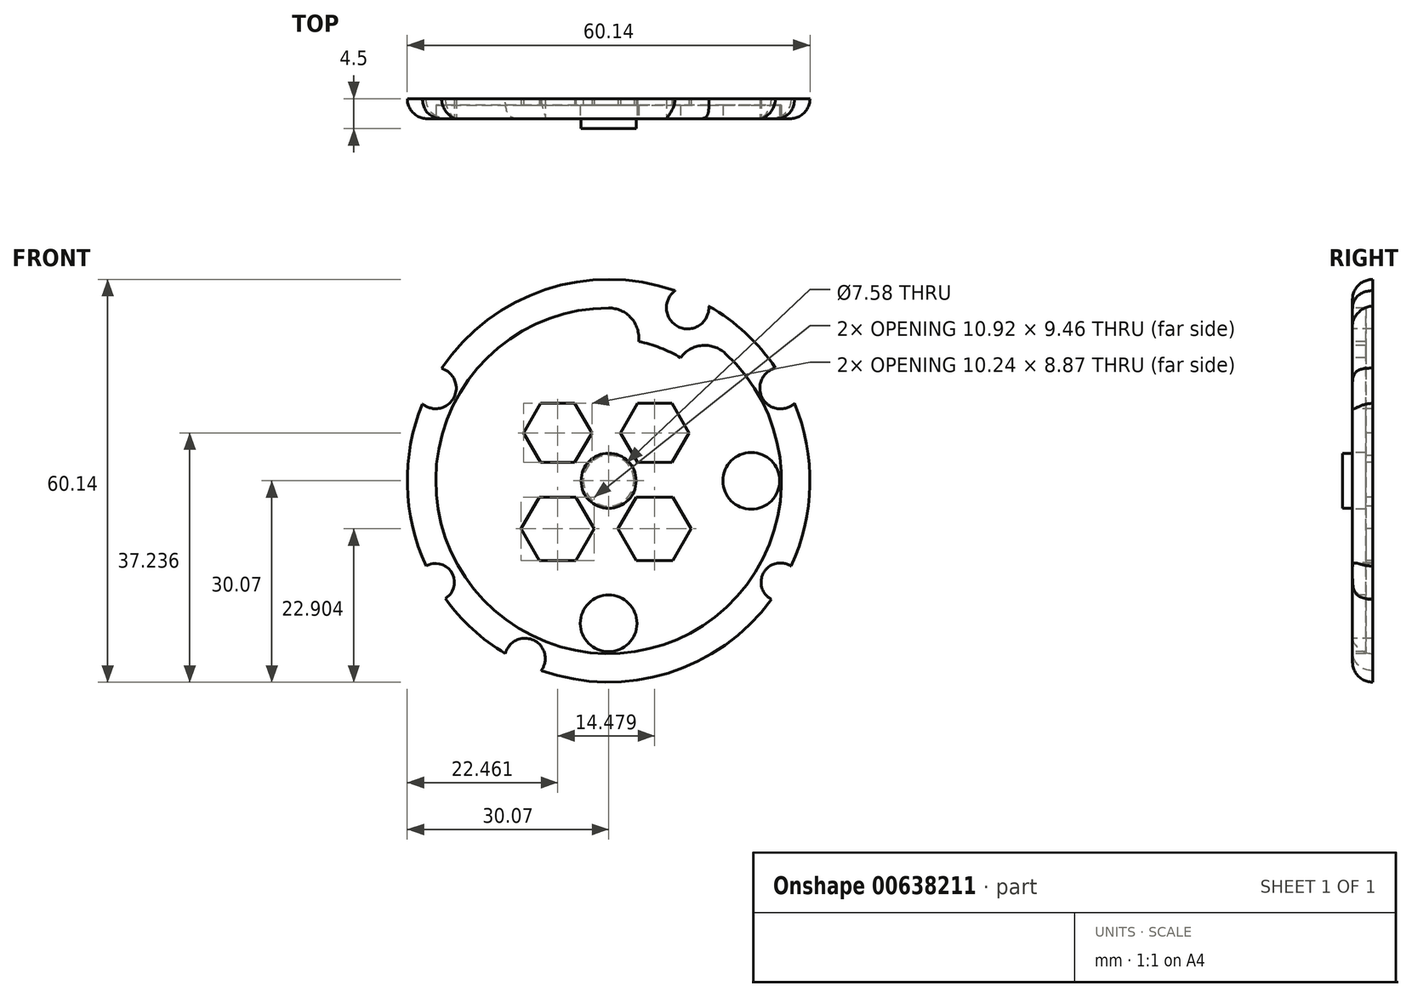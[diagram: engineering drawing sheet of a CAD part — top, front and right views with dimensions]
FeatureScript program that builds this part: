
annotation { "Feature Type Name" : "Feature", "Feature Type Description" : "" }
export const myFeature = defineFeature(function(context is Context, id is Id, definition is map)
    precondition{}
    {
        {
            var Q0;
            Q0=qCreatedBy(makeId("Front.planeOp"),FACE);
            var sketch = newSketch(context, id + "F0", { "sketchPlane" : qUnion([Q0])});
            skCircle(sketch, "E0", {"center": v(0, 0) * mm, "radius": 30.07 * mm});
            skSolve(sketch);
        }
        {
            var Q0;
            Q0=makeQuery(id+"F0.imprint","IMPRINT",FACE,{"disambiguationData":[TD([[makeQuery(id+"F0.imprint","IMPRINT",EDGE,{"derivedFrom":sQuery(id+"F0.wireOp",EDGE,"E0")}),1.0]])]});
            extrude(context, id + "F1", {"entities" : qUnion([Q0]), "depth" : 3 * mm, "offsetDistance" : 25 * mm});
        }
        {
            var Q0;
            Q0=makeQuery(id+"F1.opExtrude","CAP_FACE",FACE,{"disambiguationData":[OSD([sQuery(id+"F0.wireOp",EDGE,"E0")])],"isStart":false});
            var sketch = newSketch(context, id + "F2", { "sketchPlane" : qUnion([Q0])});
            skCircle(sketch, "E1", {"center": v(0, 0) * mm, "radius": 25.8 * mm});
            skCircle(sketch, "E2", {"center": v(0, 0) * mm, "radius": 21.3 * mm});
            skCircle(sketch, "E3", {"center": v(0, 21.3) * mm, "radius": 4.51 * mm});
            skCircle(sketch, "E4", {"center": v(21.3, 0) * mm, "radius": 4.24 * mm});
            skCircle(sketch, "E5", {"center": v(-21.3, 0) * mm, "radius": 4.2 * mm});
            skCircle(sketch, "E6", {"center": v(0, -21.3) * mm, "radius": 4.23 * mm});
            skCircle(sketch, "E7", {"center": v(14.38, 15.7) * mm, "radius": 4.51 * mm});
            skCircle(sketch, "E8", {"center": v(-14.45, -15.64) * mm, "radius": 4.25 * mm});
            skCircle(sketch, "E9", {"center": v(14.38, -15.7) * mm, "radius": 4.25 * mm});
            skCircle(sketch, "E10", {"center": v(-14.38, 15.7) * mm, "radius": 4.24 * mm});
            skSolve(sketch);
        }
        {
            var Q0;
            {var subQ0=sQuery(id+"F2.wireOp",EDGE,"E3");var subQ1=sQuery(id+"F2.wireOp",EDGE,"E2");var subQ2=makeQuery(id+"F2.imprint","INTERSECT",VERTEX,{"disambiguationData":[OD(0.0)],"derivedFrom":[subQ1,subQ0]});Q0=makeQuery(id+"F2.imprint","IMPRINT",FACE,{"disambiguationData":[TD([[makeQuery(id+"F2.imprint","IMPRINT",EDGE,{"disambiguationData":[TD([[subQ2,-1.0]])],"derivedFrom":subQ1}),-1.0]])]});}
            var Q1;
            {var subQ0=sQuery(id+"F2.wireOp",EDGE,"E3");var subQ1=sQuery(id+"F2.wireOp",EDGE,"E2");var subQ2=makeQuery(id+"F2.imprint","INTERSECT",VERTEX,{"disambiguationData":[OD(0.0)],"derivedFrom":[subQ1,subQ0]});Q1=makeQuery(id+"F2.imprint","IMPRINT",FACE,{"disambiguationData":[TD([[makeQuery(id+"F2.imprint","IMPRINT",EDGE,{"disambiguationData":[TD([[subQ2,-1.0]])],"derivedFrom":subQ1}),1.0]])]});}
            var Q2;
            {var subQ0=sQuery(id+"F2.wireOp",EDGE,"E7");var subQ1=sQuery(id+"F2.wireOp",EDGE,"E2");var subQ2=makeQuery(id+"F2.imprint","INTERSECT",VERTEX,{"disambiguationData":[OD(0.0)],"derivedFrom":[subQ1,subQ0]});Q2=makeQuery(id+"F2.imprint","IMPRINT",FACE,{"disambiguationData":[TD([[makeQuery(id+"F2.imprint","IMPRINT",EDGE,{"disambiguationData":[TD([[subQ2,-1.0]])],"derivedFrom":subQ1}),-1.0]])]});}
            var Q3;
            {var subQ0=sQuery(id+"F2.wireOp",EDGE,"E7");var subQ1=sQuery(id+"F2.wireOp",EDGE,"E2");var subQ2=makeQuery(id+"F2.imprint","INTERSECT",VERTEX,{"disambiguationData":[OD(0.0)],"derivedFrom":[subQ1,subQ0]});Q3=makeQuery(id+"F2.imprint","IMPRINT",FACE,{"disambiguationData":[TD([[makeQuery(id+"F2.imprint","IMPRINT",EDGE,{"disambiguationData":[TD([[subQ2,-1.0]])],"derivedFrom":subQ1}),1.0]])]});}
            var Q4;
            {var subQ0=sQuery(id+"F2.wireOp",EDGE,"E4");var subQ1=sQuery(id+"F2.wireOp",EDGE,"E2");var subQ2=makeQuery(id+"F2.imprint","INTERSECT",VERTEX,{"disambiguationData":[OD(0.0)],"derivedFrom":[subQ1,subQ0]});Q4=makeQuery(id+"F2.imprint","IMPRINT",FACE,{"disambiguationData":[TD([[makeQuery(id+"F2.imprint","IMPRINT",EDGE,{"disambiguationData":[TD([[subQ2,1.0]])],"derivedFrom":subQ1}),-1.0]])]});}
            var Q5;
            {var subQ0=sQuery(id+"F2.wireOp",EDGE,"E4");var subQ1=sQuery(id+"F2.wireOp",EDGE,"E2");var subQ2=makeQuery(id+"F2.imprint","INTERSECT",VERTEX,{"disambiguationData":[OD(0.0)],"derivedFrom":[subQ1,subQ0]});Q5=makeQuery(id+"F2.imprint","IMPRINT",FACE,{"disambiguationData":[TD([[makeQuery(id+"F2.imprint","IMPRINT",EDGE,{"disambiguationData":[TD([[subQ2,1.0]])],"derivedFrom":subQ1}),1.0]])]});}
            var Q6;
            {var subQ0=sQuery(id+"F2.wireOp",EDGE,"E9");var subQ1=sQuery(id+"F2.wireOp",EDGE,"E2");var subQ2=makeQuery(id+"F2.imprint","INTERSECT",VERTEX,{"disambiguationData":[OD(0.0)],"derivedFrom":[subQ1,subQ0]});Q6=makeQuery(id+"F2.imprint","IMPRINT",FACE,{"disambiguationData":[TD([[makeQuery(id+"F2.imprint","IMPRINT",EDGE,{"disambiguationData":[TD([[subQ2,-1.0]])],"derivedFrom":subQ1}),-1.0]])]});}
            var Q7;
            {var subQ0=sQuery(id+"F2.wireOp",EDGE,"E9");var subQ1=sQuery(id+"F2.wireOp",EDGE,"E2");var subQ2=makeQuery(id+"F2.imprint","INTERSECT",VERTEX,{"disambiguationData":[OD(0.0)],"derivedFrom":[subQ1,subQ0]});Q7=makeQuery(id+"F2.imprint","IMPRINT",FACE,{"disambiguationData":[TD([[makeQuery(id+"F2.imprint","IMPRINT",EDGE,{"disambiguationData":[TD([[subQ2,-1.0]])],"derivedFrom":subQ1}),1.0]])]});}
            var Q8;
            {var subQ0=sQuery(id+"F2.wireOp",EDGE,"E6");var subQ1=sQuery(id+"F2.wireOp",EDGE,"E2");var subQ2=makeQuery(id+"F2.imprint","INTERSECT",VERTEX,{"disambiguationData":[OD(0.0)],"derivedFrom":[subQ1,subQ0]});Q8=makeQuery(id+"F2.imprint","IMPRINT",FACE,{"disambiguationData":[TD([[makeQuery(id+"F2.imprint","IMPRINT",EDGE,{"disambiguationData":[TD([[subQ2,-1.0]])],"derivedFrom":subQ1}),-1.0]])]});}
            var Q9;
            {var subQ0=sQuery(id+"F2.wireOp",EDGE,"E6");var subQ1=sQuery(id+"F2.wireOp",EDGE,"E2");var subQ2=makeQuery(id+"F2.imprint","INTERSECT",VERTEX,{"disambiguationData":[OD(0.0)],"derivedFrom":[subQ1,subQ0]});Q9=makeQuery(id+"F2.imprint","IMPRINT",FACE,{"disambiguationData":[TD([[makeQuery(id+"F2.imprint","IMPRINT",EDGE,{"disambiguationData":[TD([[subQ2,-1.0]])],"derivedFrom":subQ1}),1.0]])]});}
            var Q10;
            {var subQ0=sQuery(id+"F2.wireOp",EDGE,"E8");var subQ1=sQuery(id+"F2.wireOp",EDGE,"E2");var subQ2=makeQuery(id+"F2.imprint","INTERSECT",VERTEX,{"disambiguationData":[OD(0.0)],"derivedFrom":[subQ1,subQ0]});Q10=makeQuery(id+"F2.imprint","IMPRINT",FACE,{"disambiguationData":[TD([[makeQuery(id+"F2.imprint","IMPRINT",EDGE,{"disambiguationData":[TD([[subQ2,-1.0]])],"derivedFrom":subQ1}),-1.0]])]});}
            var Q11;
            {var subQ0=sQuery(id+"F2.wireOp",EDGE,"E8");var subQ1=sQuery(id+"F2.wireOp",EDGE,"E2");var subQ2=makeQuery(id+"F2.imprint","INTERSECT",VERTEX,{"disambiguationData":[OD(0.0)],"derivedFrom":[subQ1,subQ0]});Q11=makeQuery(id+"F2.imprint","IMPRINT",FACE,{"disambiguationData":[TD([[makeQuery(id+"F2.imprint","IMPRINT",EDGE,{"disambiguationData":[TD([[subQ2,-1.0]])],"derivedFrom":subQ1}),1.0]])]});}
            var Q12;
            {var subQ0=sQuery(id+"F2.wireOp",EDGE,"E5");var subQ1=sQuery(id+"F2.wireOp",EDGE,"E2");var subQ2=makeQuery(id+"F2.imprint","INTERSECT",VERTEX,{"disambiguationData":[OD(0.0)],"derivedFrom":[subQ1,subQ0]});Q12=makeQuery(id+"F2.imprint","IMPRINT",FACE,{"disambiguationData":[TD([[makeQuery(id+"F2.imprint","IMPRINT",EDGE,{"disambiguationData":[TD([[subQ2,-1.0]])],"derivedFrom":subQ1}),1.0]])]});}
            var Q13;
            {var subQ0=sQuery(id+"F2.wireOp",EDGE,"E5");var subQ1=sQuery(id+"F2.wireOp",EDGE,"E2");var subQ2=makeQuery(id+"F2.imprint","INTERSECT",VERTEX,{"disambiguationData":[OD(0.0)],"derivedFrom":[subQ1,subQ0]});Q13=makeQuery(id+"F2.imprint","IMPRINT",FACE,{"disambiguationData":[TD([[makeQuery(id+"F2.imprint","IMPRINT",EDGE,{"disambiguationData":[TD([[subQ2,-1.0]])],"derivedFrom":subQ1}),-1.0]])]});}
            var Q14;
            {var subQ0=sQuery(id+"F2.wireOp",EDGE,"E10");var subQ1=sQuery(id+"F2.wireOp",EDGE,"E2");var subQ2=makeQuery(id+"F2.imprint","INTERSECT",VERTEX,{"disambiguationData":[OD(0.0)],"derivedFrom":[subQ1,subQ0]});Q14=makeQuery(id+"F2.imprint","IMPRINT",FACE,{"disambiguationData":[TD([[makeQuery(id+"F2.imprint","IMPRINT",EDGE,{"disambiguationData":[TD([[subQ2,-1.0]])],"derivedFrom":subQ1}),-1.0]])]});}
            var Q15;
            {var subQ0=sQuery(id+"F2.wireOp",EDGE,"E10");var subQ1=sQuery(id+"F2.wireOp",EDGE,"E2");var subQ2=makeQuery(id+"F2.imprint","INTERSECT",VERTEX,{"disambiguationData":[OD(0.0)],"derivedFrom":[subQ1,subQ0]});Q15=makeQuery(id+"F2.imprint","IMPRINT",FACE,{"disambiguationData":[TD([[makeQuery(id+"F2.imprint","IMPRINT",EDGE,{"disambiguationData":[TD([[subQ2,-1.0]])],"derivedFrom":subQ1}),1.0]])]});}
            extrude(context, id + "F3", {"entities" : qUnion([Q0, Q1, Q2, Q3, Q4, Q5, Q6, Q7, Q8, Q9, Q10, Q11, Q12, Q13, Q14, Q15]), "operationType" : NewBodyOperationType.REMOVE, "oppositeDirection" : true, "depth" : 2 * mm, "offsetDistance" : 25 * mm});
        }
        {
            var Q0;
            Q0=makeQuery(id+"F1.opExtrude","CAP_FACE",FACE,{"disambiguationData":[OSD([sQuery(id+"F0.wireOp",EDGE,"E0")])],"isStart":false});
            var sketch = newSketch(context, id + "F4", { "sketchPlane" : qUnion([Q0])});
            skCircle(sketch, "E11.cCircle", {"center": v(-7.6, 7.17) * mm, "radius": 4.43 * mm, "construction": true});
            skLineSegment(sketch, "E11.0", {"start": v(-10.17, 11.6) * mm, "end": v(-5.05, 11.6) * mm});
            skLineSegment(sketch, "E11.1", {"start": v(-5.05, 11.6) * mm, "end": v(-2.5, 7.17) * mm});
            skLineSegment(sketch, "E11.2", {"start": v(-2.5, 7.17) * mm, "end": v(-5.05, 2.73) * mm});
            skLineSegment(sketch, "E11.3", {"start": v(-5.05, 2.73) * mm, "end": v(-10.17, 2.73) * mm});
            skLineSegment(sketch, "E11.4", {"start": v(-10.17, 2.73) * mm, "end": v(-12.73, 7.17) * mm});
            skLineSegment(sketch, "E11.5", {"start": v(-12.73, 7.17) * mm, "end": v(-10.17, 11.6) * mm});
            skPoint(sketch, "E11.0.midPoint", {"position": v(-7.6, 11.6) * mm});
            skCircle(sketch, "E12.cCircle", {"center": v(6.87, 7.17) * mm, "radius": 4.43 * mm, "construction": true});
            skLineSegment(sketch, "E12.0", {"start": v(4.31, 11.6) * mm, "end": v(9.43, 11.6) * mm});
            skLineSegment(sketch, "E12.1", {"start": v(9.43, 11.6) * mm, "end": v(11.99, 7.17) * mm});
            skLineSegment(sketch, "E12.2", {"start": v(11.99, 7.17) * mm, "end": v(9.43, 2.73) * mm});
            skLineSegment(sketch, "E12.3", {"start": v(9.43, 2.73) * mm, "end": v(4.31, 2.73) * mm});
            skLineSegment(sketch, "E12.4", {"start": v(4.31, 2.73) * mm, "end": v(1.75, 7.17) * mm});
            skLineSegment(sketch, "E12.5", {"start": v(1.75, 7.17) * mm, "end": v(4.31, 11.6) * mm});
            skPoint(sketch, "E12.0.midPoint", {"position": v(6.87, 11.6) * mm});
            skCircle(sketch, "E13.cCircle", {"center": v(6.87, -7.17) * mm, "radius": 4.73 * mm, "construction": true});
            skPoint(sketch, "E13.cCircle.centerSnap0", {"position": v(6.87, 2.73) * mm});
            skLineSegment(sketch, "E13.0", {"start": v(4.14, -2.44) * mm, "end": v(9.6, -2.44) * mm});
            skLineSegment(sketch, "E13.1", {"start": v(9.6, -2.44) * mm, "end": v(12.33, -7.17) * mm});
            skLineSegment(sketch, "E13.2", {"start": v(12.33, -7.17) * mm, "end": v(9.6, -11.9) * mm});
            skLineSegment(sketch, "E13.3", {"start": v(9.6, -11.9) * mm, "end": v(4.14, -11.9) * mm});
            skLineSegment(sketch, "E13.4", {"start": v(4.14, -11.9) * mm, "end": v(1.41, -7.17) * mm});
            skLineSegment(sketch, "E13.5", {"start": v(1.41, -7.17) * mm, "end": v(4.14, -2.44) * mm});
            skPoint(sketch, "E13.0.midPoint", {"position": v(6.87, -2.44) * mm});
            skCircle(sketch, "E14.cCircle", {"center": v(-7.6, -7.17) * mm, "radius": 4.73 * mm, "construction": true});
            skPoint(sketch, "E14.cCircle.centerSnap0", {"position": v(-7.6, 2.73) * mm});
            skLineSegment(sketch, "E14.0", {"start": v(-10.34, -2.44) * mm, "end": v(-4.88, -2.44) * mm});
            skLineSegment(sketch, "E14.1", {"start": v(-4.88, -2.44) * mm, "end": v(-2.15, -7.17) * mm});
            skLineSegment(sketch, "E14.2", {"start": v(-2.15, -7.17) * mm, "end": v(-4.88, -11.9) * mm});
            skLineSegment(sketch, "E14.3", {"start": v(-4.88, -11.9) * mm, "end": v(-10.34, -11.9) * mm});
            skLineSegment(sketch, "E14.4", {"start": v(-10.34, -11.9) * mm, "end": v(-13.07, -7.17) * mm});
            skLineSegment(sketch, "E14.5", {"start": v(-13.07, -7.17) * mm, "end": v(-10.34, -2.44) * mm});
            skPoint(sketch, "E14.0.midPoint", {"position": v(-7.6, -2.44) * mm});
            skSolve(sketch);
        }
        {
            var Q0;
            Q0=makeQuery(id+"F4.imprint","IMPRINT",FACE,{"disambiguationData":[TD([[makeQuery(id+"F4.imprint","IMPRINT",EDGE,{"derivedFrom":sQuery(id+"F4.wireOp",EDGE,"E11.0")}),-1.0]])]});
            var Q1;
            Q1=makeQuery(id+"F4.imprint","IMPRINT",FACE,{"disambiguationData":[TD([[makeQuery(id+"F4.imprint","IMPRINT",EDGE,{"derivedFrom":sQuery(id+"F4.wireOp",EDGE,"E12.0")}),-1.0]])]});
            var Q2;
            Q2=makeQuery(id+"F4.imprint","IMPRINT",FACE,{"disambiguationData":[TD([[makeQuery(id+"F4.imprint","IMPRINT",EDGE,{"derivedFrom":sQuery(id+"F4.wireOp",EDGE,"E13.0")}),-1.0]])]});
            var Q3;
            Q3=makeQuery(id+"F4.imprint","IMPRINT",FACE,{"disambiguationData":[TD([[makeQuery(id+"F4.imprint","IMPRINT",EDGE,{"derivedFrom":sQuery(id+"F4.wireOp",EDGE,"E14.0")}),-1.0]])]});
            extrude(context, id + "F5", {"entities" : qUnion([Q0, Q1, Q2, Q3]), "operationType" : NewBodyOperationType.REMOVE, "oppositeDirection" : true, "depth" : 25 * mm, "offsetDistance" : 25 * mm});
        }
        {
            var Q0;
            Q0=makeQuery(id+"F1.opExtrude","CAP_FACE",FACE,{"disambiguationData":[OSD([sQuery(id+"F0.wireOp",EDGE,"E0")])],"isStart":false});
            var sketch = newSketch(context, id + "F6", { "sketchPlane" : qUnion([Q0])});
            skCircle(sketch, "E15", {"center": v(0, 0) * mm, "radius": 16.63 * mm});
            skSolve(sketch);
        }
        {
            var Q0;
            Q0=makeQuery(id+"F6.imprint","IMPRINT",FACE,{"disambiguationData":[TD([[makeQuery(id+"F6.imprint","IMPRINT",EDGE,{"derivedFrom":sQuery(id+"F6.wireOp",EDGE,"E15")}),1.0]])]});
            extrude(context, id + "F7", {"entities" : qUnion([Q0]), "operationType" : NewBodyOperationType.REMOVE, "oppositeDirection" : true, "depth" : 1.5 * mm, "offsetDistance" : 25 * mm});
        }
        {
            var Q0;
            Q0=makeQuery(id+"F1.opExtrude","CAP_FACE",FACE,{"disambiguationData":[OSD([sQuery(id+"F0.wireOp",EDGE,"E0")])],"isStart":false});
            var sketch = newSketch(context, id + "F8", { "sketchPlane" : qUnion([Q0])});
            skCircle(sketch, "E16", {"center": v(0, 0) * mm, "radius": 4.11 * mm});
            skSolve(sketch);
        }
        {
            var Q0;
            Q0=makeQuery(id+"F8.imprint","IMPRINT",FACE,{"disambiguationData":[TD([[makeQuery(id+"F8.imprint","IMPRINT",EDGE,{"derivedFrom":sQuery(id+"F8.wireOp",EDGE,"E16")}),1.0]])]});
            extrude(context, id + "F9", {"entities" : qUnion([Q0]), "operationType" : NewBodyOperationType.ADD, "depth" : 1.5 * mm, "offsetDistance" : 25 * mm});
        }
        {
            var Q0;
            Q0=makeQuery(id+"F1.opExtrude","CAP_FACE",FACE,{"disambiguationData":[OSD([sQuery(id+"F0.wireOp",EDGE,"E0")])],"isStart":false});
            var sketch = newSketch(context, id + "F10", { "sketchPlane" : qUnion([Q0])});
            skSolve(sketch);
        }
        {
            var Q0;
            Q0=makeQuery(id+"F10.imprint","IMPRINT",FACE,{"disambiguationData":[TD([[makeQuery(id+"F10.imprint","IMPRINT",EDGE,{"derivedFrom":makeQuery(id+"F1.opExtrude","CAP_EDGE",EDGE,{"disambiguationData":[OSD([sQuery(id+"F0.wireOp",EDGE,"E0")])],"isStart":false})}),1.0]])]});
            var sketch = newSketch(context, id + "F11", { "sketchPlane" : qUnion([Q0])});
            skCircle(sketch, "E17", {"center": v(0, 0) * mm, "radius": 3.79 * mm});
            skSolve(sketch);
        }
        {
            var Q0;
            Q0 = qSketchRegion(id + "F11", true);
            extrude(context, id + "F12", {"entities" : qUnion([Q0]), "operationType" : NewBodyOperationType.REMOVE, "oppositeDirection" : true, "depth" : 25 * mm, "offsetDistance" : 25 * mm});
        }
        {
            var Q0;
            Q0=makeQuery(id+"F10.imprint","IMPRINT",FACE,{"disambiguationData":[TD([[makeQuery(id+"F10.imprint","IMPRINT",EDGE,{"derivedFrom":makeQuery(id+"F1.opExtrude","CAP_EDGE",EDGE,{"disambiguationData":[OSD([sQuery(id+"F0.wireOp",EDGE,"E0")])],"isStart":false})}),1.0]])]});
            var sketch = newSketch(context, id + "F13", { "sketchPlane" : qUnion([Q0])});
            skCircle(sketch, "E18", {"center": v(-12.49, 25.85) * mm, "radius": 3.24 * mm});
            skCircle(sketch, "E19", {"center": v(11.8, 25.85) * mm, "radius": 3.16 * mm});
            skCircle(sketch, "E20", {"center": v(11.8, -26.55) * mm, "radius": 3.04 * mm});
            skCircle(sketch, "E21", {"center": v(-12.49, -26.55) * mm, "radius": 3.02 * mm});
            skSolve(sketch);
        }
        {
            var Q0;
            {var subQ0=sQuery(id+"F13.wireOp",EDGE,"E18");var subQ1=makeQuery(id+"F10.imprint","IMPRINT",EDGE,{"derivedFrom":makeQuery(id+"F1.opExtrude","CAP_EDGE",EDGE,{"disambiguationData":[OSD([sQuery(id+"F0.wireOp",EDGE,"E0")])],"isStart":false})});var subQ2=makeQuery(id+"F13.imprint","INTERSECT",VERTEX,{"disambiguationData":[OD(0.0)],"derivedFrom":[subQ1,subQ0]});Q0=makeQuery(id+"F13.imprint","IMPRINT",FACE,{"disambiguationData":[TD([[makeQuery(id+"F13.imprint","IMPRINT",EDGE,{"disambiguationData":[TD([[subQ2,-1.0]])],"derivedFrom":subQ0}),1.0]])]});}
            var Q1;
            {var subQ0=sQuery(id+"F13.wireOp",EDGE,"E19");var subQ1=makeQuery(id+"F10.imprint","IMPRINT",EDGE,{"derivedFrom":makeQuery(id+"F1.opExtrude","CAP_EDGE",EDGE,{"disambiguationData":[OSD([sQuery(id+"F0.wireOp",EDGE,"E0")])],"isStart":false})});var subQ2=makeQuery(id+"F13.imprint","INTERSECT",VERTEX,{"disambiguationData":[OD(0.0)],"derivedFrom":[subQ1,subQ0]});Q1=makeQuery(id+"F13.imprint","IMPRINT",FACE,{"disambiguationData":[TD([[makeQuery(id+"F13.imprint","IMPRINT",EDGE,{"disambiguationData":[TD([[subQ2,-1.0]])],"derivedFrom":subQ0}),1.0]])]});}
            var Q2;
            {var subQ0=sQuery(id+"F13.wireOp",EDGE,"E20");var subQ1=makeQuery(id+"F10.imprint","IMPRINT",EDGE,{"derivedFrom":makeQuery(id+"F1.opExtrude","CAP_EDGE",EDGE,{"disambiguationData":[OSD([sQuery(id+"F0.wireOp",EDGE,"E0")])],"isStart":false})});var subQ2=makeQuery(id+"F13.imprint","INTERSECT",VERTEX,{"disambiguationData":[OD(0.0)],"derivedFrom":[subQ1,subQ0]});Q2=makeQuery(id+"F13.imprint","IMPRINT",FACE,{"disambiguationData":[TD([[makeQuery(id+"F13.imprint","IMPRINT",EDGE,{"disambiguationData":[TD([[subQ2,1.0]])],"derivedFrom":subQ0}),1.0]])]});}
            var Q3;
            {var subQ0=sQuery(id+"F13.wireOp",EDGE,"E21");var subQ1=makeQuery(id+"F10.imprint","IMPRINT",EDGE,{"derivedFrom":makeQuery(id+"F1.opExtrude","CAP_EDGE",EDGE,{"disambiguationData":[OSD([sQuery(id+"F0.wireOp",EDGE,"E0")])],"isStart":false})});var subQ2=makeQuery(id+"F13.imprint","INTERSECT",VERTEX,{"disambiguationData":[OD(0.0)],"derivedFrom":[subQ1,subQ0]});Q3=makeQuery(id+"F13.imprint","IMPRINT",FACE,{"disambiguationData":[TD([[makeQuery(id+"F13.imprint","IMPRINT",EDGE,{"disambiguationData":[TD([[subQ2,1.0]])],"derivedFrom":subQ0}),1.0]])]});}
            extrude(context, id + "F14", {"entities" : qUnion([Q0, Q1, Q2, Q3]), "operationType" : NewBodyOperationType.REMOVE, "oppositeDirection" : true, "depth" : 25 * mm, "offsetDistance" : 25 * mm});
        }
        {
            var Q0;
            Q0=makeQuery(id+"F10.imprint","IMPRINT",FACE,{"disambiguationData":[TD([[makeQuery(id+"F10.imprint","IMPRINT",EDGE,{"derivedFrom":makeQuery(id+"F1.opExtrude","CAP_EDGE",EDGE,{"disambiguationData":[OSD([sQuery(id+"F0.wireOp",EDGE,"E0")])],"isStart":false})}),1.0]])]});
            var sketch = newSketch(context, id + "F15", { "sketchPlane" : qUnion([Q0])});
            skCircle(sketch, "E22", {"center": v(-25.83, 13.84) * mm, "radius": 3.07 * mm});
            skCircle(sketch, "E23", {"center": v(25.67, 13.84) * mm, "radius": 3.1 * mm});
            skCircle(sketch, "E24", {"center": v(-25.83, -15.15) * mm, "radius": 2.81 * mm});
            skCircle(sketch, "E25", {"center": v(25.65, -15.15) * mm, "radius": 2.89 * mm});
            skSolve(sketch);
        }
        {
            var Q0;
            {var subQ0=sQuery(id+"F15.wireOp",EDGE,"E23");var subQ1=makeQuery(id+"F10.imprint","IMPRINT",EDGE,{"derivedFrom":makeQuery(id+"F1.opExtrude","CAP_EDGE",EDGE,{"disambiguationData":[OSD([sQuery(id+"F0.wireOp",EDGE,"E0")])],"isStart":false})});var subQ2=makeQuery(id+"F15.imprint","INTERSECT",VERTEX,{"disambiguationData":[OD(0.0)],"derivedFrom":[subQ1,subQ0]});Q0=makeQuery(id+"F15.imprint","IMPRINT",FACE,{"disambiguationData":[TD([[makeQuery(id+"F15.imprint","IMPRINT",EDGE,{"disambiguationData":[TD([[subQ2,-1.0]])],"derivedFrom":subQ0}),1.0]])]});}
            var Q1;
            {var subQ0=sQuery(id+"F15.wireOp",EDGE,"E25");var subQ1=makeQuery(id+"F10.imprint","IMPRINT",EDGE,{"derivedFrom":makeQuery(id+"F1.opExtrude","CAP_EDGE",EDGE,{"disambiguationData":[OSD([sQuery(id+"F0.wireOp",EDGE,"E0")])],"isStart":false})});var subQ2=makeQuery(id+"F15.imprint","INTERSECT",VERTEX,{"disambiguationData":[OD(0.0)],"derivedFrom":[subQ1,subQ0]});Q1=makeQuery(id+"F15.imprint","IMPRINT",FACE,{"disambiguationData":[TD([[makeQuery(id+"F15.imprint","IMPRINT",EDGE,{"disambiguationData":[TD([[subQ2,1.0]])],"derivedFrom":subQ0}),1.0]])]});}
            var Q2;
            {var subQ0=sQuery(id+"F15.wireOp",EDGE,"E24");var subQ1=makeQuery(id+"F10.imprint","IMPRINT",EDGE,{"derivedFrom":makeQuery(id+"F1.opExtrude","CAP_EDGE",EDGE,{"disambiguationData":[OSD([sQuery(id+"F0.wireOp",EDGE,"E0")])],"isStart":false})});var subQ2=makeQuery(id+"F15.imprint","INTERSECT",VERTEX,{"disambiguationData":[OD(0.0)],"derivedFrom":[subQ1,subQ0]});Q2=makeQuery(id+"F15.imprint","IMPRINT",FACE,{"disambiguationData":[TD([[makeQuery(id+"F15.imprint","IMPRINT",EDGE,{"disambiguationData":[TD([[subQ2,1.0]])],"derivedFrom":subQ0}),1.0]])]});}
            var Q3;
            {var subQ0=sQuery(id+"F15.wireOp",EDGE,"E22");var subQ1=makeQuery(id+"F10.imprint","IMPRINT",EDGE,{"derivedFrom":makeQuery(id+"F1.opExtrude","CAP_EDGE",EDGE,{"disambiguationData":[OSD([sQuery(id+"F0.wireOp",EDGE,"E0")])],"isStart":false})});var subQ2=makeQuery(id+"F15.imprint","INTERSECT",VERTEX,{"disambiguationData":[OD(0.0)],"derivedFrom":[subQ1,subQ0]});Q3=makeQuery(id+"F15.imprint","IMPRINT",FACE,{"disambiguationData":[TD([[makeQuery(id+"F15.imprint","IMPRINT",EDGE,{"disambiguationData":[TD([[subQ2,-1.0]])],"derivedFrom":subQ0}),1.0]])]});}
            extrude(context, id + "F16", {"entities" : qUnion([Q0, Q1, Q2, Q3]), "operationType" : NewBodyOperationType.REMOVE, "oppositeDirection" : true, "depth" : 25 * mm, "offsetDistance" : 25 * mm});
        }
        {
            var Q0;
            {var subQ0=sQuery(id+"F0.wireOp",EDGE,"E0");Q0=makeQuery(id+"F14.boolean.opBoolean","SPLIT",EDGE,{"disambiguationData":[TD([makeQuery(id+"F1.opExtrude","SWEPT_FACE",FACE,{"disambiguationData":[OSD([subQ0])]}),makeQuery(id+"F1.opExtrude","CAP_FACE",FACE,{"disambiguationData":[OSD([subQ0])],"isStart":false}),makeQuery(id+"F14.opExtrude","SWEPT_FACE",FACE,{"disambiguationData":[OSD([sQuery(id+"F13.wireOp",EDGE,"E18")])]}),makeQuery(id+"F14.opExtrude","SWEPT_FACE",FACE,{"disambiguationData":[OSD([sQuery(id+"F13.wireOp",EDGE,"E19")])]})])],"derivedFrom":makeQuery(id+"F1.opExtrude","CAP_EDGE",EDGE,{"disambiguationData":[OSD([subQ0])],"isStart":false})});}
            var Q1;
            {var subQ0=sQuery(id+"F0.wireOp",EDGE,"E0");var subQ1=makeQuery(id+"F1.opExtrude","SWEPT_FACE",FACE,{"disambiguationData":[OSD([subQ0])]});var subQ2=makeQuery(id+"F14.opExtrude","SWEPT_FACE",FACE,{"disambiguationData":[OSD([sQuery(id+"F13.wireOp",EDGE,"E19")])]});var subQ3=makeQuery(id+"F1.opExtrude","CAP_FACE",FACE,{"disambiguationData":[OSD([subQ0])],"isStart":false});Q1=makeQuery(id+"F16.boolean.opBoolean","SPLIT",EDGE,{"disambiguationData":[TD([subQ1,subQ3,makeQuery(id+"F14.boolean.opBoolean","COPY",FACE,{"derivedFrom":subQ2}),makeQuery(id+"F16.opExtrude","SWEPT_FACE",FACE,{"disambiguationData":[OSD([sQuery(id+"F15.wireOp",EDGE,"E23")])]})])],"derivedFrom":makeQuery(id+"F14.boolean.opBoolean","SPLIT",EDGE,{"disambiguationData":[TD([subQ1,subQ3,subQ2,makeQuery(id+"F14.opExtrude","SWEPT_FACE",FACE,{"disambiguationData":[OSD([sQuery(id+"F13.wireOp",EDGE,"E20")])]})])],"derivedFrom":makeQuery(id+"F1.opExtrude","CAP_EDGE",EDGE,{"disambiguationData":[OSD([subQ0])],"isStart":false})})});}
            var Q2;
            {var subQ0=sQuery(id+"F0.wireOp",EDGE,"E0");var subQ1=makeQuery(id+"F1.opExtrude","SWEPT_FACE",FACE,{"disambiguationData":[OSD([subQ0])]});var subQ2=makeQuery(id+"F1.opExtrude","CAP_FACE",FACE,{"disambiguationData":[OSD([subQ0])],"isStart":false});Q2=makeQuery(id+"F16.boolean.opBoolean","SPLIT",EDGE,{"disambiguationData":[TD([subQ1,subQ2,makeQuery(id+"F16.opExtrude","SWEPT_FACE",FACE,{"disambiguationData":[OSD([sQuery(id+"F15.wireOp",EDGE,"E23")])]}),makeQuery(id+"F16.opExtrude","SWEPT_FACE",FACE,{"disambiguationData":[OSD([sQuery(id+"F15.wireOp",EDGE,"E25")])]})])],"derivedFrom":makeQuery(id+"F14.boolean.opBoolean","SPLIT",EDGE,{"disambiguationData":[TD([subQ1,subQ2,makeQuery(id+"F14.opExtrude","SWEPT_FACE",FACE,{"disambiguationData":[OSD([sQuery(id+"F13.wireOp",EDGE,"E19")])]}),makeQuery(id+"F14.opExtrude","SWEPT_FACE",FACE,{"disambiguationData":[OSD([sQuery(id+"F13.wireOp",EDGE,"E20")])]})])],"derivedFrom":makeQuery(id+"F1.opExtrude","CAP_EDGE",EDGE,{"disambiguationData":[OSD([subQ0])],"isStart":false})})});}
            var Q3;
            {var subQ0=sQuery(id+"F0.wireOp",EDGE,"E0");var subQ1=makeQuery(id+"F1.opExtrude","SWEPT_FACE",FACE,{"disambiguationData":[OSD([subQ0])]});var subQ2=makeQuery(id+"F1.opExtrude","CAP_FACE",FACE,{"disambiguationData":[OSD([subQ0])],"isStart":false});var subQ3=makeQuery(id+"F14.opExtrude","SWEPT_FACE",FACE,{"disambiguationData":[OSD([sQuery(id+"F13.wireOp",EDGE,"E20")])]});Q3=makeQuery(id+"F16.boolean.opBoolean","SPLIT",EDGE,{"disambiguationData":[TD([subQ1,subQ2,makeQuery(id+"F14.boolean.opBoolean","COPY",FACE,{"derivedFrom":subQ3}),makeQuery(id+"F16.opExtrude","SWEPT_FACE",FACE,{"disambiguationData":[OSD([sQuery(id+"F15.wireOp",EDGE,"E25")])]})])],"derivedFrom":makeQuery(id+"F14.boolean.opBoolean","SPLIT",EDGE,{"disambiguationData":[TD([subQ1,subQ2,makeQuery(id+"F14.opExtrude","SWEPT_FACE",FACE,{"disambiguationData":[OSD([sQuery(id+"F13.wireOp",EDGE,"E19")])]}),subQ3])],"derivedFrom":makeQuery(id+"F1.opExtrude","CAP_EDGE",EDGE,{"disambiguationData":[OSD([subQ0])],"isStart":false})})});}
            var Q4;
            {var subQ0=sQuery(id+"F0.wireOp",EDGE,"E0");Q4=makeQuery(id+"F14.boolean.opBoolean","SPLIT",EDGE,{"disambiguationData":[TD([makeQuery(id+"F1.opExtrude","SWEPT_FACE",FACE,{"disambiguationData":[OSD([subQ0])]}),makeQuery(id+"F1.opExtrude","CAP_FACE",FACE,{"disambiguationData":[OSD([subQ0])],"isStart":false}),makeQuery(id+"F14.opExtrude","SWEPT_FACE",FACE,{"disambiguationData":[OSD([sQuery(id+"F13.wireOp",EDGE,"E20")])]}),makeQuery(id+"F14.opExtrude","SWEPT_FACE",FACE,{"disambiguationData":[OSD([sQuery(id+"F13.wireOp",EDGE,"E21")])]})])],"derivedFrom":makeQuery(id+"F1.opExtrude","CAP_EDGE",EDGE,{"disambiguationData":[OSD([subQ0])],"isStart":false})});}
            var Q5;
            {var subQ0=sQuery(id+"F0.wireOp",EDGE,"E0");var subQ1=makeQuery(id+"F1.opExtrude","SWEPT_FACE",FACE,{"disambiguationData":[OSD([subQ0])]});var subQ2=makeQuery(id+"F1.opExtrude","CAP_FACE",FACE,{"disambiguationData":[OSD([subQ0])],"isStart":false});var subQ3=makeQuery(id+"F14.opExtrude","SWEPT_FACE",FACE,{"disambiguationData":[OSD([sQuery(id+"F13.wireOp",EDGE,"E21")])]});Q5=makeQuery(id+"F16.boolean.opBoolean","SPLIT",EDGE,{"disambiguationData":[TD([subQ1,subQ2,makeQuery(id+"F14.boolean.opBoolean","COPY",FACE,{"derivedFrom":subQ3}),makeQuery(id+"F16.opExtrude","SWEPT_FACE",FACE,{"disambiguationData":[OSD([sQuery(id+"F15.wireOp",EDGE,"E24")])]})])],"derivedFrom":makeQuery(id+"F14.boolean.opBoolean","SPLIT",EDGE,{"disambiguationData":[TD([subQ1,subQ2,makeQuery(id+"F14.opExtrude","SWEPT_FACE",FACE,{"disambiguationData":[OSD([sQuery(id+"F13.wireOp",EDGE,"E18")])]}),subQ3])],"derivedFrom":makeQuery(id+"F1.opExtrude","CAP_EDGE",EDGE,{"disambiguationData":[OSD([subQ0])],"isStart":false})})});}
            var Q6;
            {var subQ0=sQuery(id+"F0.wireOp",EDGE,"E0");var subQ1=makeQuery(id+"F1.opExtrude","SWEPT_FACE",FACE,{"disambiguationData":[OSD([subQ0])]});var subQ2=makeQuery(id+"F1.opExtrude","CAP_FACE",FACE,{"disambiguationData":[OSD([subQ0])],"isStart":false});Q6=makeQuery(id+"F16.boolean.opBoolean","SPLIT",EDGE,{"disambiguationData":[TD([subQ1,subQ2,makeQuery(id+"F16.opExtrude","SWEPT_FACE",FACE,{"disambiguationData":[OSD([sQuery(id+"F15.wireOp",EDGE,"E22")])]}),makeQuery(id+"F16.opExtrude","SWEPT_FACE",FACE,{"disambiguationData":[OSD([sQuery(id+"F15.wireOp",EDGE,"E24")])]})])],"derivedFrom":makeQuery(id+"F14.boolean.opBoolean","SPLIT",EDGE,{"disambiguationData":[TD([subQ1,subQ2,makeQuery(id+"F14.opExtrude","SWEPT_FACE",FACE,{"disambiguationData":[OSD([sQuery(id+"F13.wireOp",EDGE,"E18")])]}),makeQuery(id+"F14.opExtrude","SWEPT_FACE",FACE,{"disambiguationData":[OSD([sQuery(id+"F13.wireOp",EDGE,"E21")])]})])],"derivedFrom":makeQuery(id+"F1.opExtrude","CAP_EDGE",EDGE,{"disambiguationData":[OSD([subQ0])],"isStart":false})})});}
            var Q7;
            {var subQ0=sQuery(id+"F0.wireOp",EDGE,"E0");var subQ1=makeQuery(id+"F1.opExtrude","SWEPT_FACE",FACE,{"disambiguationData":[OSD([subQ0])]});var subQ2=makeQuery(id+"F1.opExtrude","CAP_FACE",FACE,{"disambiguationData":[OSD([subQ0])],"isStart":false});var subQ3=makeQuery(id+"F14.opExtrude","SWEPT_FACE",FACE,{"disambiguationData":[OSD([sQuery(id+"F13.wireOp",EDGE,"E18")])]});Q7=makeQuery(id+"F16.boolean.opBoolean","SPLIT",EDGE,{"disambiguationData":[TD([subQ1,subQ2,makeQuery(id+"F14.boolean.opBoolean","COPY",FACE,{"derivedFrom":subQ3}),makeQuery(id+"F16.opExtrude","SWEPT_FACE",FACE,{"disambiguationData":[OSD([sQuery(id+"F15.wireOp",EDGE,"E22")])]})])],"derivedFrom":makeQuery(id+"F14.boolean.opBoolean","SPLIT",EDGE,{"disambiguationData":[TD([subQ1,subQ2,subQ3,makeQuery(id+"F14.opExtrude","SWEPT_FACE",FACE,{"disambiguationData":[OSD([sQuery(id+"F13.wireOp",EDGE,"E21")])]})])],"derivedFrom":makeQuery(id+"F1.opExtrude","CAP_EDGE",EDGE,{"disambiguationData":[OSD([subQ0])],"isStart":false})})});}
            fillet(context, id + "F17", {"entities" : qUnion([Q0, Q1, Q2, Q3, Q4, Q5, Q6, Q7]), "radius" : 3 * mm, "tangentPropagation" : true, "allowEdgeOverflow" : false});
        }
    });
